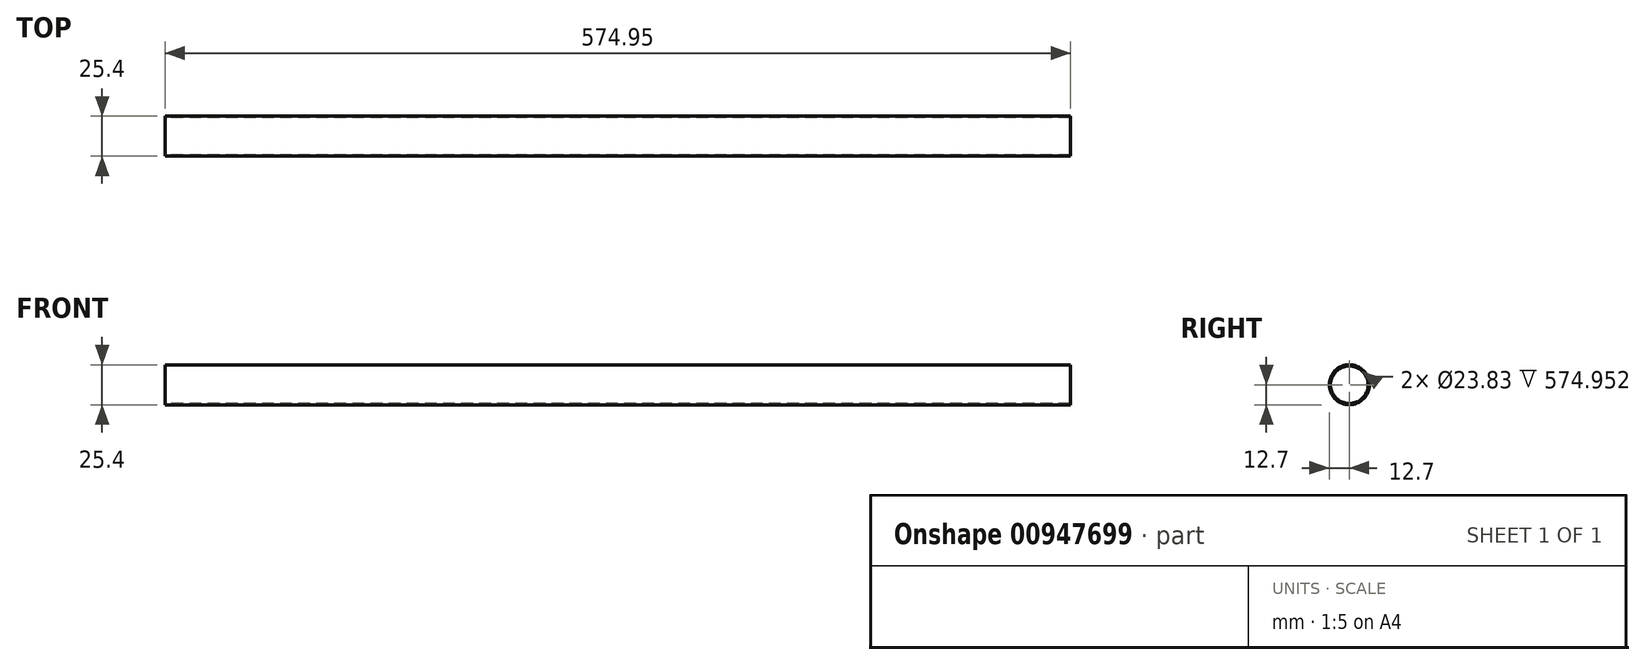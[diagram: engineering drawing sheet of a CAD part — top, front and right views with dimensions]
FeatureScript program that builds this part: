
annotation { "Feature Type Name" : "Feature", "Feature Type Description" : "" }
export const myFeature = defineFeature(function(context is Context, id is Id, definition is map)
    precondition{}
    {
        {
            var Q0;
            Q0=qCreatedBy(makeId("Right.planeOp"),FACE);
            var sketch = newSketch(context, id + "F0", { "sketchPlane" : qUnion([Q0])});
            skCircle(sketch, "E0", {"center": v(0, 0) * mm, "radius": 12.7 * mm});
            skCircle(sketch, "E1", {"center": v(0, 0) * mm, "radius": 11.91 * mm});
            skSolve(sketch);
        }
        {
            var Q0;
            Q0 = qSketchRegion(id + "F0", true);
            extrude(context, id + "F1", {"entities" : qUnion([Q0]), "depth" : 574.95 * mm, "offsetDistance" : 25 * mm});
        }
    });
